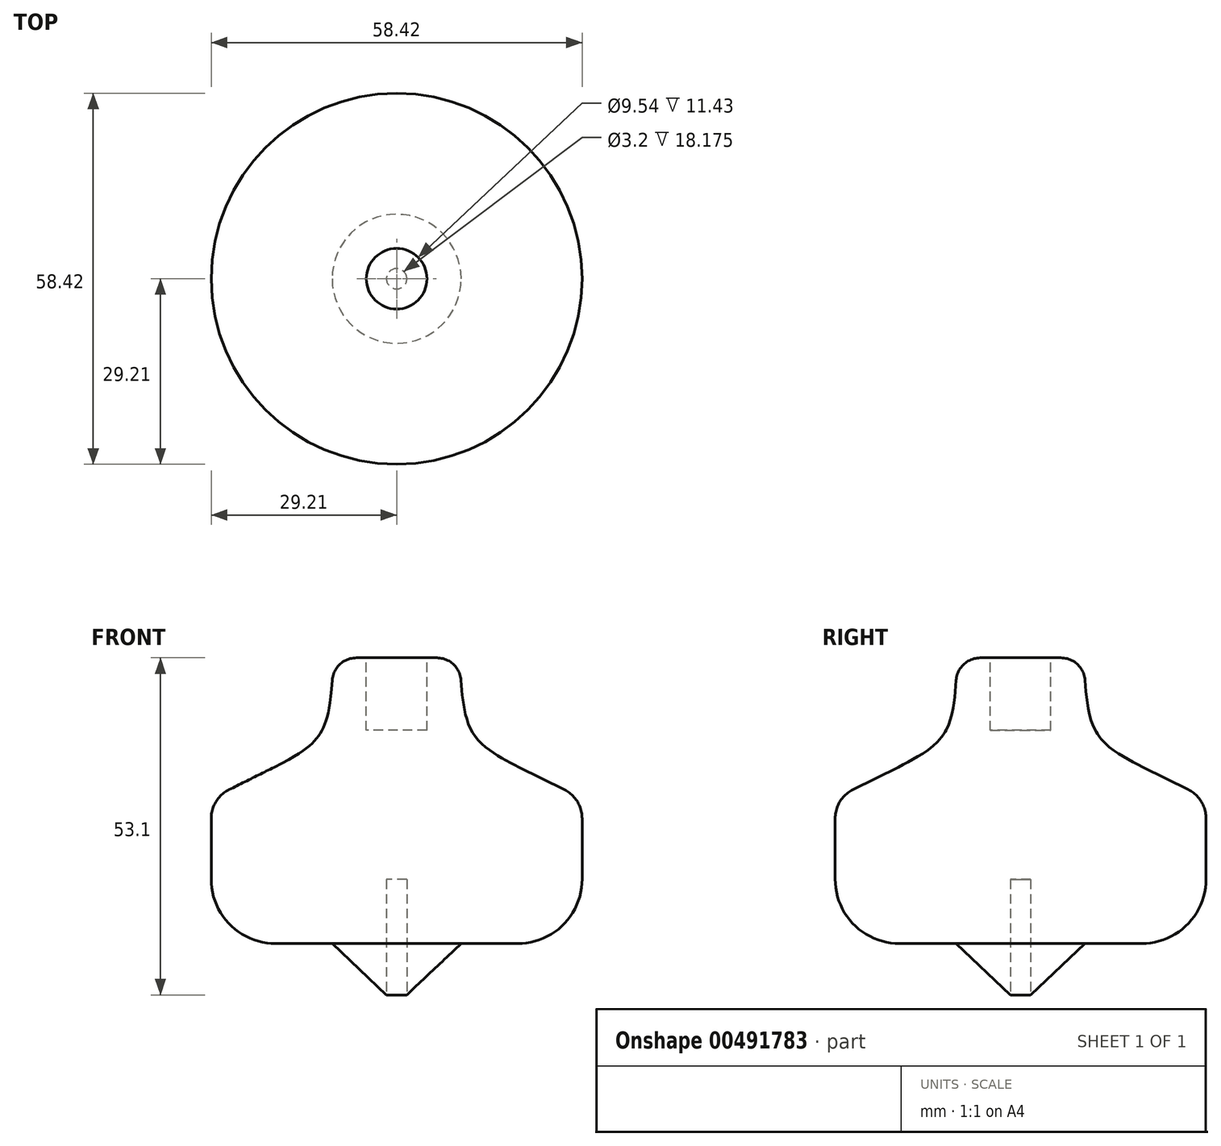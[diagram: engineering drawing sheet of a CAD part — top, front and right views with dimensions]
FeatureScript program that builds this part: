
annotation { "Feature Type Name" : "Feature", "Feature Type Description" : "" }
export const myFeature = defineFeature(function(context is Context, id is Id, definition is map)
    precondition{}
    {
        {
            var Q0;
            Q0=qCreatedBy(makeId("Front.planeOp"),FACE);
            var sketch = newSketch(context, id + "F0", { "sketchPlane" : qUnion([Q0])});
            skLineSegment(sketch, "E0", {"start": v(0, 0) * mm, "end": v(10.16, 9.59) * mm});
            skLineSegment(sketch, "E1", {"start": v(29.21, 9.59) * mm, "end": v(10.16, 9.59) * mm});
            skLineSegment(sketch, "E2", {"start": v(29.21, 9.59) * mm, "end": v(29.21, 32.45) * mm});
            skLineSegment(sketch, "E3", {"start": v(29.21, 32.45) * mm, "end": v(10.16, 41.91) * mm});
            skLineSegment(sketch, "E4", {"start": v(10.16, 41.91) * mm, "end": v(10.16, 54.61) * mm});
            skLineSegment(sketch, "E5", {"start": v(10.16, 54.61) * mm, "end": v(0, 54.61) * mm});
            skLineSegment(sketch, "E6", {"start": v(0, 54.6) * mm, "end": v(0, 0) * mm});
            skLineSegment(sketch, "E7", {"start": v(0, 0) * mm, "end": v(0, 54.6) * mm});
            skSolve(sketch);
        }
        {
            var Q0;
            Q0=makeQuery(id+"F0.imprint","IMPRINT",FACE,{"disambiguationData":[TD([[makeQuery(id+"F0.imprint","IMPRINT",EDGE,{"derivedFrom":sQuery(id+"F0.wireOp",EDGE,"E0")}),1.0]])]});
            var Q1;
            Q1=sQuery(id+"F0.wireOp",EDGE,"E7");
            revolve(context, id + "F1", {"entities" : qUnion([Q0]), "axis" : qUnion([Q1]), "revolveType" : RevolveType.FULL});
        }
        {
            var Q0;
            Q0=makeQuery(id+"F1.opRevolve","SWEPT_EDGE",EDGE,{"disambiguationData":[OSD([sQuery(id+"F0.wireOp",EDGE,"E1"),sQuery(id+"F0.wireOp",EDGE,"E2")])]});
            fillet(context, id + "F2", {"entities" : qUnion([Q0]), "radius" : 10.16 * mm, "tangentPropagation" : true, "allowEdgeOverflow" : false});
        }
        {
            var Q0;
            Q0=makeQuery(id+"F1.opRevolve","SWEPT_EDGE",EDGE,{"disambiguationData":[OSD([sQuery(id+"F0.wireOp",EDGE,"E2"),sQuery(id+"F0.wireOp",EDGE,"E3")])]});
            fillet(context, id + "F3", {"entities" : qUnion([Q0]), "radius" : 5.08 * mm, "tangentPropagation" : true, "allowEdgeOverflow" : false});
        }
        {
            var Q0;
            Q0=makeQuery(id+"F1.opRevolve","SWEPT_FACE",FACE,{"disambiguationData":[OSD([sQuery(id+"F0.wireOp",EDGE,"E5")])]});
            var sketch = newSketch(context, id + "F4", { "sketchPlane" : qUnion([Q0])});
            skCircle(sketch, "E8", {"center": v(0, 0) * mm, "radius": 4.77 * mm});
            skSolve(sketch);
        }
        {
            var Q0;
            Q0=makeQuery(id+"F4.imprint","IMPRINT",FACE,{"disambiguationData":[TD([[makeQuery(id+"F4.imprint","IMPRINT",EDGE,{"derivedFrom":sQuery(id+"F4.wireOp",EDGE,"E8")}),1.0]])]});
            var Q1;
            Q1=sQuery(id+"F4.wireOp",EDGE,"E8");
            extrude(context, id + "F5", {"entities" : qUnion([Q0]), "operationType" : NewBodyOperationType.REMOVE, "surfaceEntities" : qUnion([Q1]), "oppositeDirection" : true, "depth" : 11.43 * mm});
        }
        {
            var Q0;
            Q0=qCreatedBy(makeId("Top.planeOp"),FACE);
            var sketch = newSketch(context, id + "F6", { "sketchPlane" : qUnion([Q0])});
            skCircle(sketch, "E9", {"center": v(0, 0) * mm, "radius": 1.6 * mm});
            skSolve(sketch);
        }
        {
            var Q0;
            Q0=makeQuery(id+"F6.imprint","IMPRINT",FACE,{"disambiguationData":[TD([[makeQuery(id+"F6.imprint","IMPRINT",EDGE,{"derivedFrom":sQuery(id+"F6.wireOp",EDGE,"E9")}),1.0]])]});
            var Q1;
            Q1=sQuery(id+"F6.wireOp",EDGE,"E9");
            extrude(context, id + "F7", {"entities" : qUnion([Q0]), "operationType" : NewBodyOperationType.REMOVE, "surfaceEntities" : qUnion([Q1]), "depth" : 19.68 * mm});
        }
        {
            var Q0;
            Q0=makeQuery(id+"F1.opRevolve","SWEPT_EDGE",EDGE,{"disambiguationData":[OSD([sQuery(id+"F0.wireOp",EDGE,"E4"),sQuery(id+"F0.wireOp",EDGE,"E5")])]});
            fillet(context, id + "F8", {"entities" : qUnion([Q0]), "radius" : 3.8 * mm, "tangentPropagation" : true, "allowEdgeOverflow" : false});
        }
        {
            var Q0;
            Q0=makeQuery(id+"F1.opRevolve","SWEPT_FACE",FACE,{"disambiguationData":[OSD([sQuery(id+"F0.wireOp",EDGE,"E4")])]});
            fillet(context, id + "F9", {"entities" : qUnion([Q0]), "radius" : 16.5 * mm, "tangentPropagation" : true, "rho" : 0.65, "crossSection" : FilletCrossSection.CONIC, "allowEdgeOverflow" : false});
        }
    });
